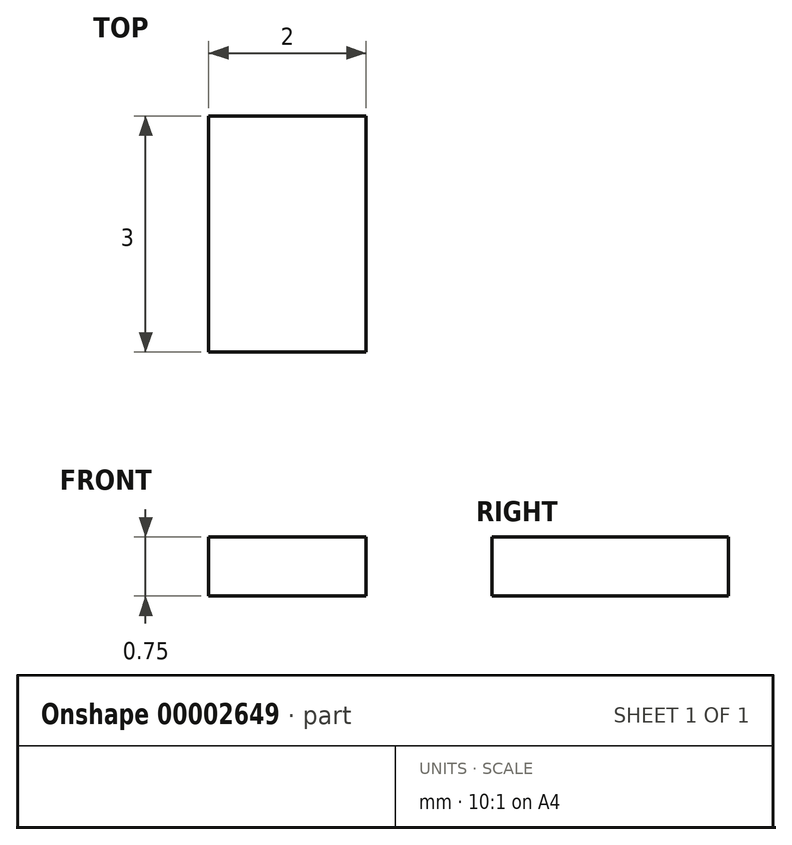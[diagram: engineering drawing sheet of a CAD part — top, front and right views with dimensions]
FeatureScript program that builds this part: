
annotation { "Feature Type Name" : "Feature", "Feature Type Description" : "" }
export const myFeature = defineFeature(function(context is Context, id is Id, definition is map)
    precondition{}
    {
        {
            var Q0;
            Q0=qCreatedBy(makeId("Top.planeOp"),FACE);
            var sketch = newSketch(context, id + "F0", { "sketchPlane" : qUnion([Q0])});
            skLineSegment(sketch, "E0.bottom", {"start": v(-10.94, -6.14) * mm, "end": v(-8.94, -6.14) * mm});
            skLineSegment(sketch, "E0.top", {"start": v(-10.94, -9.14) * mm, "end": v(-8.94, -9.14) * mm});
            skLineSegment(sketch, "E0.left", {"start": v(-10.94, -6.14) * mm, "end": v(-10.94, -9.14) * mm});
            skLineSegment(sketch, "E0.right", {"start": v(-8.94, -6.14) * mm, "end": v(-8.94, -9.14) * mm});
            skSolve(sketch);
        }
        {
            var Q0;
            Q0=makeQuery(id+"F0.imprint","IMPRINT",FACE,{"disambiguationData":[TD([[makeQuery(id+"F0.imprint","IMPRINT",EDGE,{"derivedFrom":sQuery(id+"F0.wireOp",EDGE,"E0.bottom")}),-1.0]])]});
            extrude(context, id + "F1", {"entities" : qUnion([Q0]), "depth" : .75 * mm});
        }
    });
